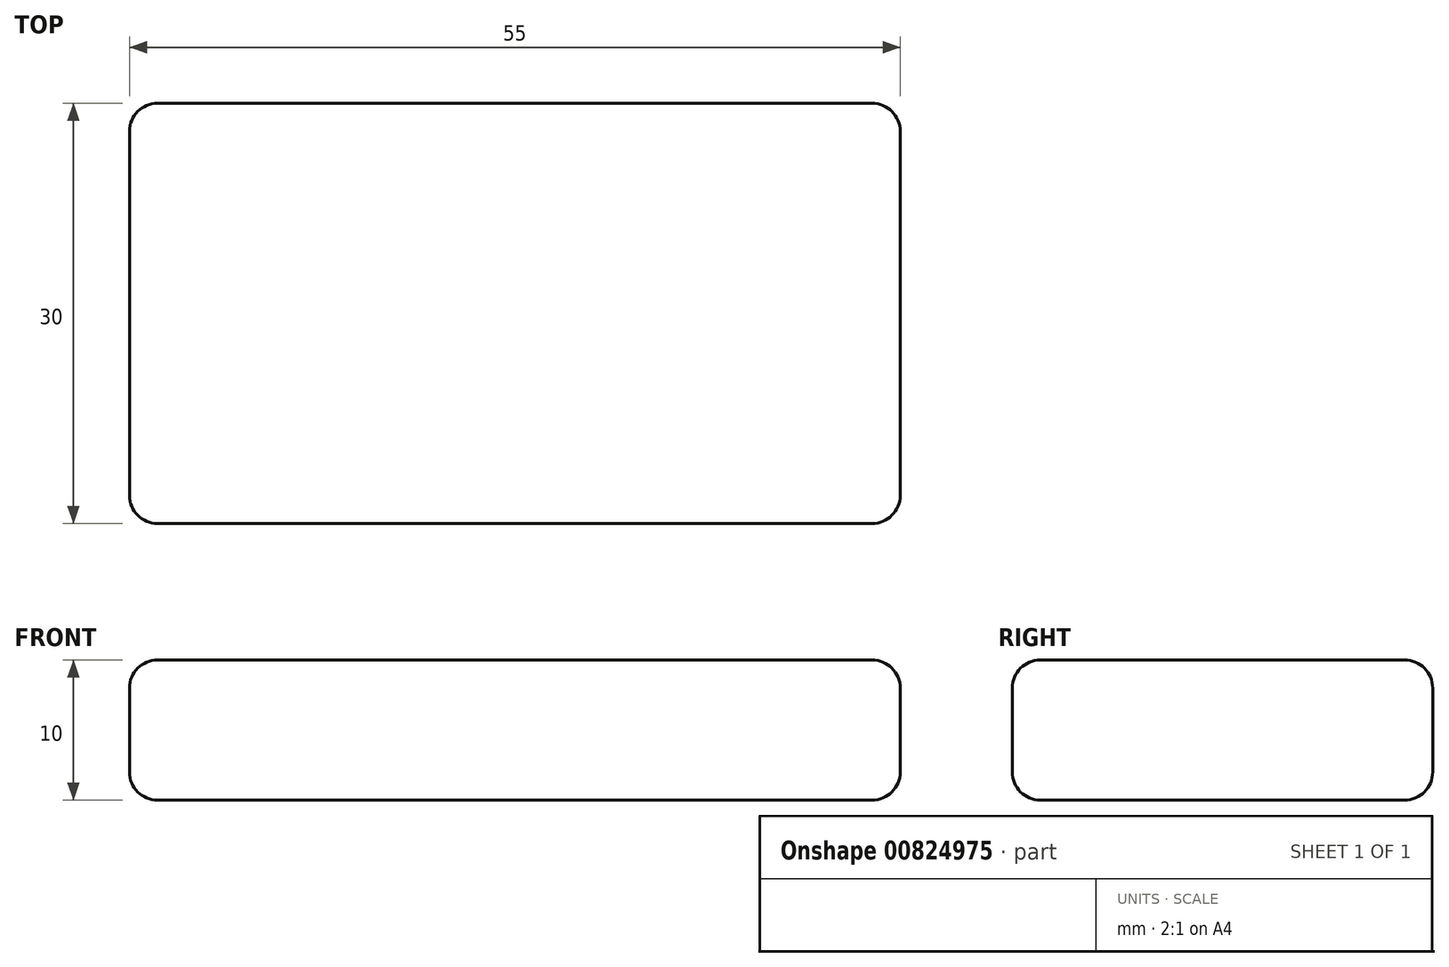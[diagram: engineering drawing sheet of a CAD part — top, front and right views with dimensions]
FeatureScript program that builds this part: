
annotation { "Feature Type Name" : "Feature", "Feature Type Description" : "" }
export const myFeature = defineFeature(function(context is Context, id is Id, definition is map)
    precondition{}
    {
        {
            var Q0;
            Q0=qCreatedBy(makeId("Top.planeOp"),FACE);
            var sketch = newSketch(context, id + "F0", { "sketchPlane" : qUnion([Q0])});
            skLineSegment(sketch, "E0.bottom", {"start": v(-27.5, 15) * mm, "end": v(27.5, 15) * mm});
            skLineSegment(sketch, "E0.top", {"start": v(-27.5, -15) * mm, "end": v(27.5, -15) * mm});
            skLineSegment(sketch, "E0.left", {"start": v(-27.5, 15) * mm, "end": v(-27.5, -15) * mm});
            skLineSegment(sketch, "E0.right", {"start": v(27.5, 15) * mm, "end": v(27.5, -15) * mm});
            skPoint(sketch, "E0.middle", {"position": v(0, 0) * mm});
            skSolve(sketch);
        }
        {
            var Q0;
            Q0=makeQuery(id+"F0.imprint","IMPRINT",FACE,{"disambiguationData":[TD([[makeQuery(id+"F0.imprint","IMPRINT",EDGE,{"derivedFrom":sQuery(id+"F0.wireOp",EDGE,"E0.bottom")}),-1.0]])]});
            extrude(context, id + "F1", {"entities" : qUnion([Q0]), "depth" : 10 * mm, "offsetDistance" : 25 * mm});
        }
        {
            var Q0;
            Q0=makeQuery(id+"F1.opExtrude","CAP_EDGE",EDGE,{"disambiguationData":[OSD([sQuery(id+"F0.wireOp",EDGE,"E0.right")])],"isStart":true});
            var Q1;
            Q1=makeQuery(id+"F1.opExtrude","CAP_EDGE",EDGE,{"disambiguationData":[OSD([sQuery(id+"F0.wireOp",EDGE,"E0.right")])],"isStart":false});
            fillet(context, id + "F2", {"entities" : qUnion([Q0, Q1]), "radius" : 2 * mm, "tangentPropagation" : true, "allowEdgeOverflow" : false});
        }
        {
            var Q0;
            Q0=makeQuery(id+"F1.opExtrude","CAP_EDGE",EDGE,{"disambiguationData":[OSD([sQuery(id+"F0.wireOp",EDGE,"E0.left")])],"isStart":false});
            var Q1;
            Q1=makeQuery(id+"F1.opExtrude","CAP_EDGE",EDGE,{"disambiguationData":[OSD([sQuery(id+"F0.wireOp",EDGE,"E0.left")])],"isStart":true});
            var Q2;
            Q2=makeQuery(id+"F1.opExtrude","SWEPT_EDGE",EDGE,{"disambiguationData":[OSD([sQuery(id+"F0.wireOp",EDGE,"E0.top"),sQuery(id+"F0.wireOp",EDGE,"E0.left")])]});
            var Q3;
            Q3=makeQuery(id+"F1.opExtrude","SWEPT_EDGE",EDGE,{"disambiguationData":[OSD([sQuery(id+"F0.wireOp",EDGE,"E0.top"),sQuery(id+"F0.wireOp",EDGE,"E0.right")])]});
            var Q4;
            Q4=makeQuery(id+"F1.opExtrude","SWEPT_FACE",FACE,{"disambiguationData":[OSD([sQuery(id+"F0.wireOp",EDGE,"E0.bottom")])]});
            fillet(context, id + "F3", {"entities" : qUnion([Q0, Q1, Q2, Q3, Q4]), "radius" : 2 * mm, "tangentPropagation" : true, "allowEdgeOverflow" : false});
        }
    });
